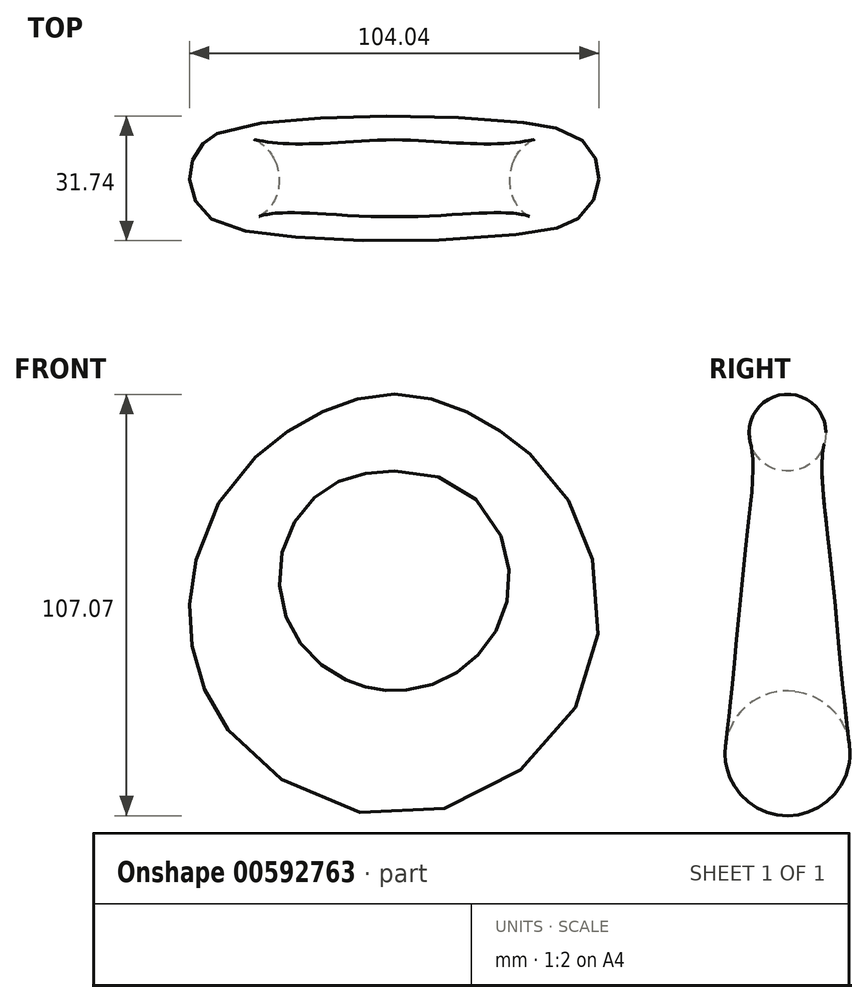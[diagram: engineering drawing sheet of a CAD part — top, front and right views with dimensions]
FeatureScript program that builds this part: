
annotation { "Feature Type Name" : "Feature", "Feature Type Description" : "" }
export const myFeature = defineFeature(function(context is Context, id is Id, definition is map)
    precondition{}
    {
        {
            var Q0;
            Q0=qCreatedBy(makeId("Front.planeOp"),FACE);
            var sketch = newSketch(context, id + "F0", { "sketchPlane" : qUnion([Q0])});
            skCircle(sketch, "E0", {"center": v(0, -1.15) * mm, "radius": 40.43 * mm});
            skSolve(sketch);
        }
        {
            var Q0;
            Q0=qCreatedBy(makeId("Right.planeOp"),FACE);
            var sketch = newSketch(context, id + "F1", { "sketchPlane" : qUnion([Q0])});
            skCircle(sketch, "E1", {"center": v(0, 40.27) * mm, "radius": 9.78 * mm});
            skCircle(sketch, "E2", {"center": v(0, -41.16) * mm, "radius": 15.87 * mm});
            skSolve(sketch);
        }
        {
            var Q0;
            Q0=sQuery(id+"F0.wireOp",EDGE,"E0");
            var Q1;
            Q1=makeQuery(id+"F1.imprint","IMPRINT",FACE,{"disambiguationData":[TD([[makeQuery(id+"F1.imprint","IMPRINT",EDGE,{"derivedFrom":sQuery(id+"F1.wireOp",EDGE,"E1")}),1.0]])]});
            var Q2;
            Q2=makeQuery(id+"F1.imprint","IMPRINT",FACE,{"disambiguationData":[TD([[makeQuery(id+"F1.imprint","IMPRINT",EDGE,{"derivedFrom":sQuery(id+"F1.wireOp",EDGE,"E2")}),1.0]])]});
            var Q3;
            Q3=sQuery(id+"F1.wireOp",EDGE,"E1");
            var Q4;
            Q4=sQuery(id+"F1.wireOp",EDGE,"E2");
            loft(context, id + "F2", {"bodyType" : ToolBodyType.SURFACE, "addSections" : true, "spine" : qUnion([Q0]), "sectionCount" : 5, "sheetProfilesArray" : [{ "sheetProfileEntities" : qUnion([Q1]) }, { "sheetProfileEntities" : qUnion([Q2]) }], "wireProfilesArray" : [{ "wireProfileEntities" : qUnion([Q3]) }, { "wireProfileEntities" : qUnion([Q4]) }]});
        }
    });
